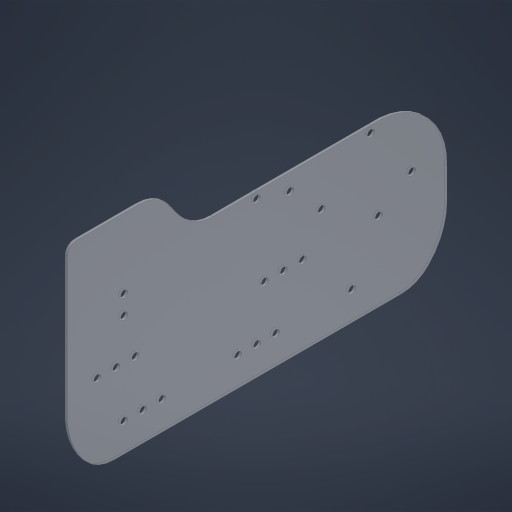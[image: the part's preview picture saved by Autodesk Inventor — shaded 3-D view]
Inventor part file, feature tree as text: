
AUTODESK INVENTOR PART (.ipt)
format: ipt  version: 2024 (Build 280153000, 153)  size: 338,944 bytes
history: native  units: in
note: dims shown in document units (in); Inventor stores cm internally (conversion verified against a paired STEP export)
features: sketch x1, extrude x1, hole x1
ambient origin geometry x8: Origin, YZ Plane, XZ Plane, XY Plane, X Axis, Y Axis, Z Axis, Center Point
bodies: Solid1 (feature_tree)
feature tree (3):
  sketch  "Sketch1"  dims[d4=0.0625in d5=0.0in d81=1.325in d82=1.5in d86=0.5in d93=1.0in d94=1.5in d95=1.5in d98=1.325in d102=0.1875in d103=0.75in d104=0.375in d105=0.25in d106=0.5635in d107=1.0in d108=0.8108in d109=1.5in d110=0.5in d111=0.5in d112=1.5in d113=1.75in d114=0.5in d115=0.5in d116=1.325in d117=1.0in d118=0.0in d119=0.25in d120=0.25in d122=0.75in d126=5.0in d127=2.5in d129=1.5in d130=0.875in d131=0.875in d132=1.5in d133=1.972in d134=1.0in d135=1.0in d137=1.25in d138=2.875in d139=1.0in d140=4.0in d141=1.5in d142=1.0in d143=0.25in d144=2.4602in d145=5.0in d148=0.875in d149=0.575in d153=0.25in d154=0.5in d155=0.5in d157=0.5in d158=0.25in d159=0.0625in d160=3.0in d161=0.2in d162=0.875in d163=1.5in d164=1.0in]
  extrude  "Extrusion1"  Depth=1.0in
  hole  "Hole4"  [1 undecoded]
note: 1 required parameter value undecoded (feature->parameter linkage not recoverable at this tier; creation-order binding heuristic only, values carry confidence <= 0.55)
